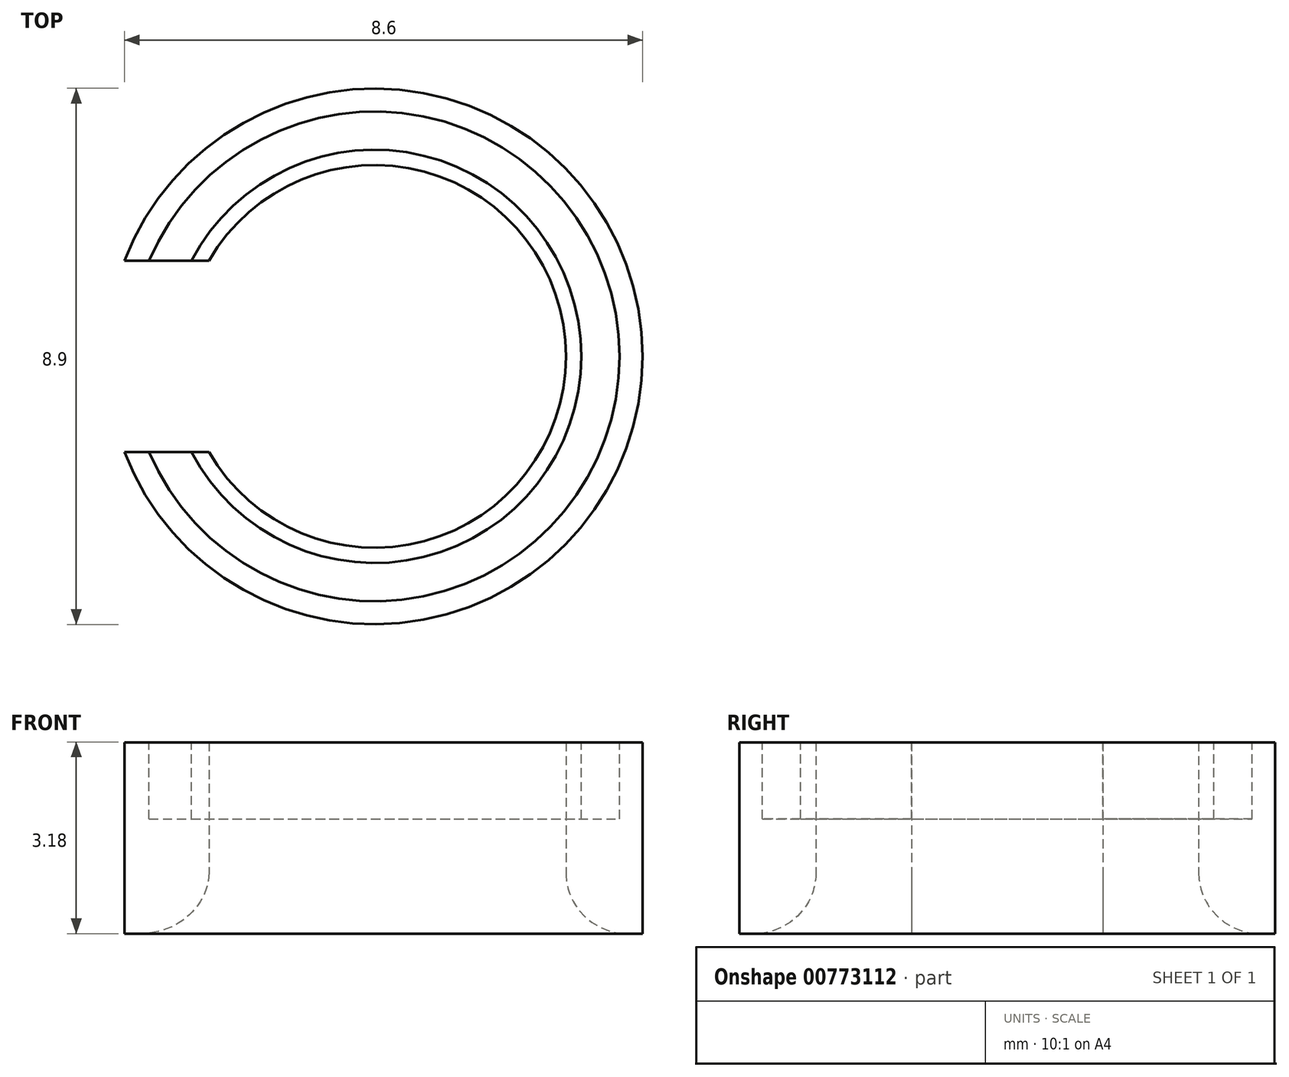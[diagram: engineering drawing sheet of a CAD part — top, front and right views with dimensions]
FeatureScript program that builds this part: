
annotation { "Feature Type Name" : "Feature", "Feature Type Description" : "" }
export const myFeature = defineFeature(function(context is Context, id is Id, definition is map)
    precondition{}
    {
        {
            var Q0;
            Q0=qCreatedBy(makeId("Top.planeOp"),FACE);
            var sketch = newSketch(context, id + "F0", { "sketchPlane" : qUnion([Q0])});
            skCircle(sketch, "E0", {"center": v(0, 0) * mm, "radius": 4.45 * mm});
            skCircle(sketch, "E1", {"center": v(0, 0) * mm, "radius": 3.17 * mm});
            skSolve(sketch);
        }
        {
            var Q0;
            Q0 = qSketchRegion(id + "F0", true);
            extrude(context, id + "F1", {"entities" : qUnion([Q0]), "depth" : 3.17 * mm, "offsetDistance" : 25.4 * mm});
        }
        {
            var Q0;
            Q0=makeQuery(id+"F1.opExtrude","CAP_FACE",FACE,{"disambiguationData":[OSD([sQuery(id+"F0.wireOp",EDGE,"E0"),sQuery(id+"F0.wireOp",EDGE,"E1")])],"isStart":false});
            var sketch = newSketch(context, id + "F2", { "sketchPlane" : qUnion([Q0])});
            skCircle(sketch, "E2", {"center": v(0, 0) * mm, "radius": 3.43 * mm});
            skCircle(sketch, "E3", {"center": v(0, 0) * mm, "radius": 4.06 * mm});
            skSolve(sketch);
        }
        {
            var Q0;
            Q0 = qSketchRegion(id + "F2", true);
            extrude(context, id + "F3", {"entities" : qUnion([Q0]), "operationType" : NewBodyOperationType.REMOVE, "oppositeDirection" : true, "depth" : 1.27 * mm, "offsetDistance" : 25.4 * mm});
        }
        {
            var Q0;
            Q0=makeQuery(id+"F1.opExtrude","CAP_EDGE",EDGE,{"disambiguationData":[OSD([sQuery(id+"F0.wireOp",EDGE,"E1")])],"isStart":true});
            fillet(context, id + "F4", {"entities" : qUnion([Q0]), "radius" : 1.02 * mm, "tangentPropagation" : true, "allowEdgeOverflow" : false});
        }
        {
            var Q0;
            Q0=qCreatedBy(makeId("Top.planeOp"),FACE);
            var sketch = newSketch(context, id + "F5", { "sketchPlane" : qUnion([Q0])});
            skLineSegment(sketch, "E4.bottom", {"start": v(0, 1.59) * mm, "end": v(-6.35, 1.59) * mm});
            skLineSegment(sketch, "E4.top", {"start": v(0, -1.59) * mm, "end": v(-6.35, -1.59) * mm});
            skLineSegment(sketch, "E4.left", {"start": v(0, 1.59) * mm, "end": v(0, -1.59) * mm});
            skLineSegment(sketch, "E4.right", {"start": v(-6.35, 1.59) * mm, "end": v(-6.35, -1.59) * mm});
            skSolve(sketch);
        }
        {
            var Q0;
            Q0 = qSketchRegion(id + "F5", true);
            extrude(context, id + "F6", {"entities" : qUnion([Q0]), "operationType" : NewBodyOperationType.REMOVE, "depth" : 25.4 * mm, "offsetDistance" : 25.4 * mm});
        }
    });
